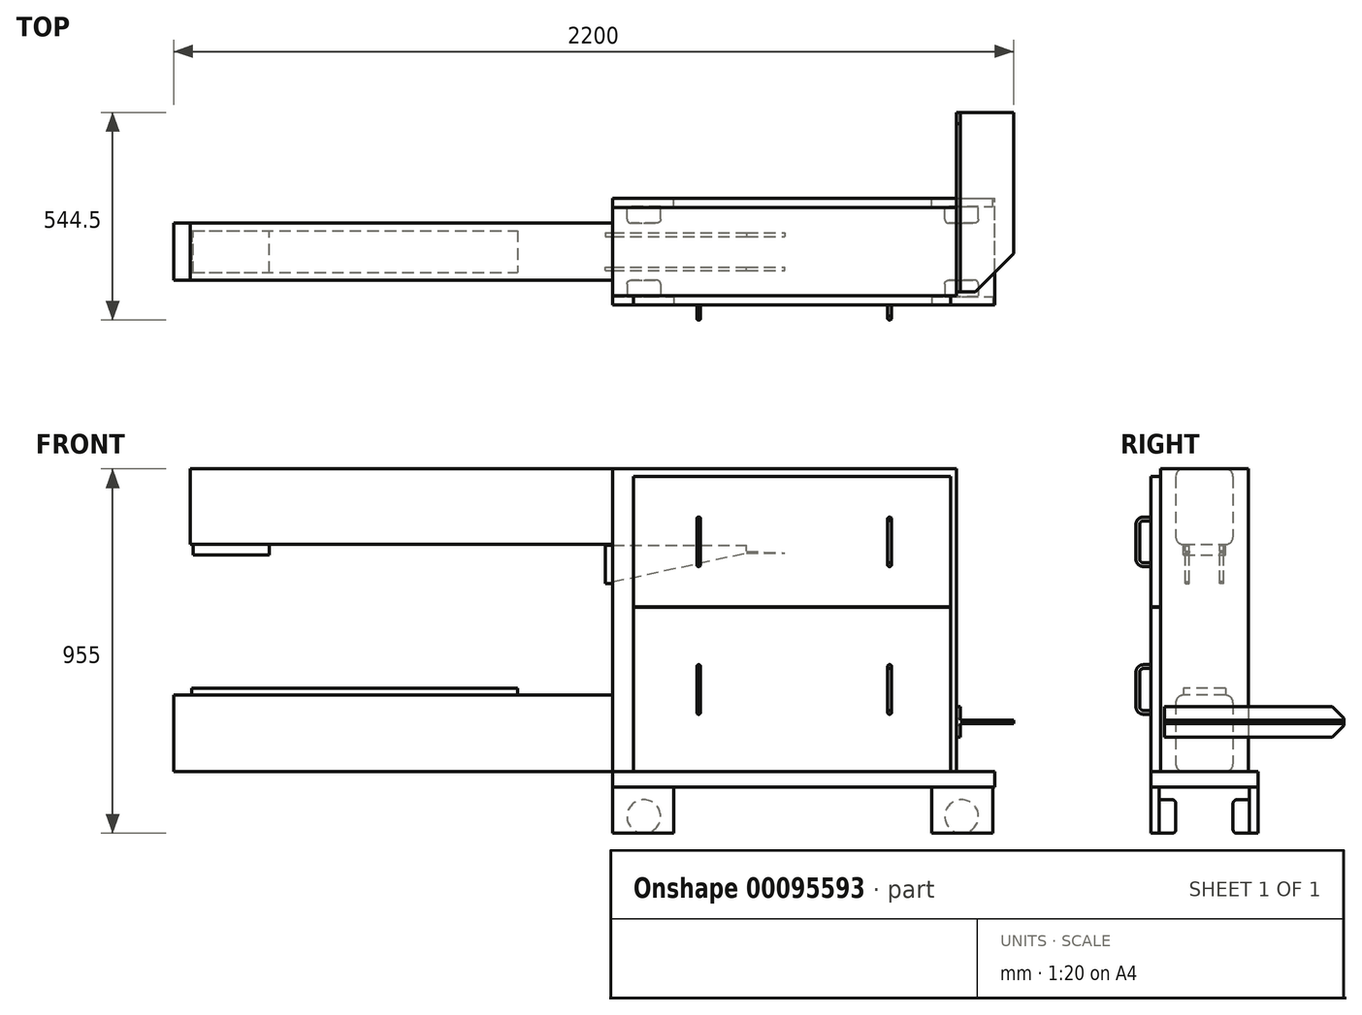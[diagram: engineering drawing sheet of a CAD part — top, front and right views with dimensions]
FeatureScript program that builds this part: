
annotation { "Feature Type Name" : "Feature", "Feature Type Description" : "" }
export const myFeature = defineFeature(function(context is Context, id is Id, definition is map)
    precondition{}
    {
        {
            var Q0;
            Q0=qCreatedBy(makeId("Front.planeOp"),FACE);
            var sketch = newSketch(context, id + "F0", { "sketchPlane" : qUnion([Q0])});
            skLineSegment(sketch, "E0.rect.bottom", {"start": v(-575, 100) * mm, "end": v(575, 100) * mm});
            skLineSegment(sketch, "E0.rect.top", {"start": v(-575, -100) * mm, "end": v(1475, -100) * mm});
            skLineSegment(sketch, "E0.rect.left", {"start": v(-575, 100) * mm, "end": v(-575, -100) * mm});
            skLineSegment(sketch, "E0.rect.right", {"start": v(575, 100) * mm, "end": v(575, -100) * mm});
            skPoint(sketch, "E0.rect.middle", {"position": v(0, 0) * mm});
            skLineSegment(sketch, "E1.0", {"start": v(-532, 495) * mm, "end": v(575, 495) * mm});
            skLineSegment(sketch, "E2.0", {"start": v(-532, 693) * mm, "end": v(1475, 693) * mm});
            skLineSegment(sketch, "E3.0", {"start": v(-532, 693) * mm, "end": v(-532, 495) * mm});
            skLineSegment(sketch, "E4", {"start": v(575, 693) * mm, "end": v(575, -100) * mm});
            skLineSegment(sketch, "E5.0", {"start": v(1475, 693) * mm, "end": v(1475, -100) * mm});
            skSolve(sketch);
        }
        {
            var Q0;
            {var subQ3=sQuery(id+"F0.wireOp",EDGE,"E1.0");Q0=makeQuery(id+"F0.imprint","IMPRINT",FACE,{"disambiguationData":[TD([[makeQuery(id+"F0.imprint","IMPRINT",EDGE,{"derivedFrom":subQ3}),1.0]])]});}
            var Q1;
            {var subQ3=sQuery(id+"F0.wireOp",EDGE,"E0.rect.bottom");Q1=makeQuery(id+"F0.imprint","IMPRINT",FACE,{"disambiguationData":[TD([[makeQuery(id+"F0.imprint","IMPRINT",EDGE,{"derivedFrom":subQ3}),-1.0]])]});}
            extrude(context, id + "F1", {"entities" : qUnion([Q0, Q1]), "endBound" : BoundingType.SYMMETRIC, "depth" : 150 * mm});
        }
        {
            var Q0;
            {var subQ0=sQuery(id+"F0.wireOp",EDGE,"E5.0");Q0=makeQuery(id+"F0.imprint","IMPRINT",FACE,{"disambiguationData":[TD([[makeQuery(id+"F0.imprint","IMPRINT",EDGE,{"derivedFrom":subQ0}),-1.0]])]});}
            extrude(context, id + "F2", {"entities" : qUnion([Q0]), "endBound" : BoundingType.SYMMETRIC, "depth" : 230 * mm});
        }
        {
            var Q0;
            Q0=makeQuery(id+"F1.opExtrude","CAP_EDGE",EDGE,{"disambiguationData":[OSD([sQuery(id+"F0.wireOp",EDGE,"E0.rect.bottom")])],"isStart":false});
            var Q1;
            Q1=makeQuery(id+"F1.opExtrude","CAP_EDGE",EDGE,{"disambiguationData":[OSD([sQuery(id+"F0.wireOp",EDGE,"E0.rect.top")])],"isStart":false});
            var Q2;
            Q2=makeQuery(id+"F1.opExtrude","CAP_EDGE",EDGE,{"disambiguationData":[OSD([sQuery(id+"F0.wireOp",EDGE,"E1.0")])],"isStart":false});
            var Q3;
            Q3=makeQuery(id+"F1.opExtrude","CAP_EDGE",EDGE,{"disambiguationData":[OSD([sQuery(id+"F0.wireOp",EDGE,"E2.0")])],"isStart":false});
            var Q4;
            Q4=makeQuery(id+"F1.opExtrude","CAP_EDGE",EDGE,{"disambiguationData":[OSD([sQuery(id+"F0.wireOp",EDGE,"E2.0")])],"isStart":true});
            var Q5;
            Q5=makeQuery(id+"F1.opExtrude","CAP_EDGE",EDGE,{"disambiguationData":[OSD([sQuery(id+"F0.wireOp",EDGE,"E1.0")])],"isStart":true});
            var Q6;
            Q6=makeQuery(id+"F1.opExtrude","CAP_EDGE",EDGE,{"disambiguationData":[OSD([sQuery(id+"F0.wireOp",EDGE,"E0.rect.bottom")])],"isStart":true});
            var Q7;
            Q7=makeQuery(id+"F1.opExtrude","CAP_EDGE",EDGE,{"disambiguationData":[OSD([sQuery(id+"F0.wireOp",EDGE,"E0.rect.top")])],"isStart":true});
            fillet(context, id + "F3", {"entities" : qUnion([Q0, Q1, Q2, Q3, Q4, Q5, Q6, Q7]), "radius" : 20 * mm, "tangentPropagation" : true, "allowEdgeOverflow" : false});
        }
        {
            var Q0;
            Q0=makeQuery(id+"F1.opExtrude","SWEPT_FACE",FACE,{"disambiguationData":[OSD([sQuery(id+"F0.wireOp",EDGE,"E0.rect.bottom")])]});
            var sketch = newSketch(context, id + "F4", { "sketchPlane" : qUnion([Q0])});
            skLineSegment(sketch, "E6.0", {"start": v(-528, -55) * mm, "end": v(-528, 55) * mm, "construction": true});
            skLineSegment(sketch, "E7.0", {"start": v(326, -55) * mm, "end": v(326, 55) * mm, "construction": true});
            skLineSegment(sketch, "E8.bottom", {"start": v(-528, 55) * mm, "end": v(326, 55) * mm});
            skLineSegment(sketch, "E8.top", {"start": v(-528, -55) * mm, "end": v(326, -55) * mm});
            skLineSegment(sketch, "E8.left", {"start": v(-528, 55) * mm, "end": v(-528, -55) * mm});
            skLineSegment(sketch, "E8.right", {"start": v(326, 55) * mm, "end": v(326, -55) * mm});
            skSolve(sketch);
        }
        {
            var Q0;
            Q0=qSketchRegion(id+"F4",true);
            extrude(context, id + "F5", {"entities" : qUnion([Q0]), "operationType" : NewBodyOperationType.ADD, "depth" : 18 * mm});
        }
        {
            var Q0;
            Q0=makeQuery(id+"F1.opExtrude","SWEPT_FACE",FACE,{"disambiguationData":[OSD([sQuery(id+"F0.wireOp",EDGE,"E1.0")])]});
            var sketch = newSketch(context, id + "F6", { "sketchPlane" : qUnion([Q0])});
            skLineSegment(sketch, "E9.0", {"start": v(-524, 55) * mm, "end": v(-524, -55) * mm, "construction": true});
            skLineSegment(sketch, "E10.0", {"start": v(-324, 55) * mm, "end": v(-324, -55) * mm, "construction": true});
            skLineSegment(sketch, "E11.bottom", {"start": v(-524, 55) * mm, "end": v(-324, 55) * mm});
            skLineSegment(sketch, "E11.top", {"start": v(-524, -55) * mm, "end": v(-324, -55) * mm});
            skLineSegment(sketch, "E11.left", {"start": v(-524, 55) * mm, "end": v(-524, -55) * mm});
            skLineSegment(sketch, "E11.right", {"start": v(-324, 55) * mm, "end": v(-324, -55) * mm});
            skSolve(sketch);
        }
        {
            var Q0;
            Q0=qSketchRegion(id+"F6",true);
            extrude(context, id + "F7", {"entities" : qUnion([Q0]), "operationType" : NewBodyOperationType.ADD, "depth" : 27 * mm});
        }
        {
            var Q0;
            Q0=qCreatedBy(makeId("Front.planeOp"),FACE);
            cPlane(context, id + "F8", {"entities" : qUnion([Q0]), "cplaneType" : CPlaneType.OFFSET, "offset" : 40 * mm, "width" : 150 * mm, "height" : 150 * mm});
        }
        {
            var Q0;
            Q0=qCreatedBy(id+"F8.planeOp",FACE);
            var sketch = newSketch(context, id + "F9", { "sketchPlane" : qUnion([Q0])});
            skLineSegment(sketch, "E12.0", {"start": v(-532, 495) * mm, "end": v(575, 495) * mm, "construction": true});
            skLineSegment(sketch, "E13.0", {"start": v(575, 693) * mm, "end": v(575, -100) * mm, "construction": true});
            skLineSegment(sketch, "E14.0", {"start": v(-575, 100) * mm, "end": v(575, 100) * mm, "construction": true});
            skLineSegment(sketch, "E15.0", {"start": v(475, 693) * mm, "end": v(475, -100) * mm, "construction": true});
            skLineSegment(sketch, "E16.0", {"start": v(-1025.5, 200) * mm, "end": v(1025.5, 200) * mm, "construction": true});
            skLineSegment(sketch, "E17", {"start": v(575, 296.5) * mm, "end": v(528.06, 296.5) * mm, "construction": true});
            skLineSegment(sketch, "E18.bottom", {"start": v(555, 200) * mm, "end": v(575, 200) * mm});
            skLineSegment(sketch, "E18.top", {"start": v(575, 100) * mm, "end": v(925.5, 100) * mm});
            skLineSegment(sketch, "E18.left", {"start": v(925.5, 120) * mm, "end": v(925.5, 100) * mm});
            skLineSegment(sketch, "E18.right", {"start": v(575, 200) * mm, "end": v(575, 100) * mm, "construction": true});
            skLineSegment(sketch, "E19.0", {"start": v(555, 200) * mm, "end": v(555, 100) * mm, "construction": true});
            skLineSegment(sketch, "E20.0", {"start": v(925.5, 120) * mm, "end": v(1025.5, 120) * mm, "construction": true});
            skLineSegment(sketch, "E21", {"start": v(555, 100) * mm, "end": v(1025.5, 120) * mm});
            skLineSegment(sketch, "E22", {"start": v(555, 200) * mm, "end": v(925.5, 120) * mm});
            skLineSegment(sketch, "E23", {"start": v(1025.5, 200) * mm, "end": v(1025.5, 120) * mm});
            skLineSegment(sketch, "E24.MirrorCS", {"start": v(555, 393) * mm, "end": v(575, 393) * mm});
            skLineSegment(sketch, "E25.MirrorCS", {"start": v(555, 493) * mm, "end": v(1025.5, 473) * mm});
            skLineSegment(sketch, "E26.MirrorCS", {"start": v(925.5, 473) * mm, "end": v(925.5, 493) * mm});
            skLineSegment(sketch, "E27.MirrorCS", {"start": v(575, 393) * mm, "end": v(575, 493) * mm});
            skLineSegment(sketch, "E28.MirrorCS", {"start": v(1025.5, 393) * mm, "end": v(1025.5, 473) * mm});
            skLineSegment(sketch, "E29.MirrorCS", {"start": v(555, 393) * mm, "end": v(925.5, 473) * mm});
            skLineSegment(sketch, "E30.MirrorCS", {"start": v(925.5, 473) * mm, "end": v(1025.5, 473) * mm});
            skLineSegment(sketch, "E31.MirrorCS", {"start": v(575, 493) * mm, "end": v(925.5, 493) * mm});
            skLineSegment(sketch, "E32.MirrorCS", {"start": v(555, 393) * mm, "end": v(555, 493) * mm});
            skSolve(sketch);
        }
        {
            var Q0;
            Q0=qSketchRegion(id+"F9",true);
            extrude(context, id + "F10", {"entities" : qUnion([Q0]), "depth" : 10 * mm});
        }
        {
            var Q0;
            Q0=makeQuery(id+"F10.opExtrude","SWEPT_BODY",BODY,{"disambiguationData":[OSD([sQuery(id+"F9.wireOp",EDGE,"E24.MirrorCS"),sQuery(id+"F9.wireOp",EDGE,"E26.MirrorCS"),sQuery(id+"F9.wireOp",EDGE,"E27.MirrorCS"),sQuery(id+"F9.wireOp",EDGE,"E28.MirrorCS"),sQuery(id+"F9.wireOp",EDGE,"E29.MirrorCS"),sQuery(id+"F9.wireOp",EDGE,"E31.MirrorCS")])]});
            var Q1;
            Q1=makeQuery(id+"F10.opExtrude","SWEPT_BODY",BODY,{"disambiguationData":[OSD([sQuery(id+"F9.wireOp",EDGE,"E18.bottom"),sQuery(id+"F9.wireOp",EDGE,"E18.top"),sQuery(id+"F9.wireOp",EDGE,"E18.left"),sQuery(id+"F9.wireOp",EDGE,"E21"),sQuery(id+"F9.wireOp",EDGE,"E22"),sQuery(id+"F9.wireOp",EDGE,"E23")])]});
            var Q2;
            Q2=qCreatedBy(makeId("Front.planeOp"),FACE);
            mirror(context, id + "F11", {"entities" : qUnion([Q0, Q1]), "mirrorPlane" : qUnion([Q2])});
        }
        {
            var Q0;
            Q0=makeQuery(id+"F2.opExtrude","CAP_FACE",FACE,{"disambiguationData":[OSD([sQuery(id+"F0.wireOp",EDGE,"E0.rect.top"),sQuery(id+"F0.wireOp",EDGE,"E2.0"),sQuery(id+"F0.wireOp",EDGE,"E4"),sQuery(id+"F0.wireOp",EDGE,"E5.0")])],"isStart":false});
            var sketch = newSketch(context, id + "F12", { "sketchPlane" : qUnion([Q0])});
            skLineSegment(sketch, "E33.0", {"start": v(-982.5, 673) * mm, "end": v(1925.5, 673) * mm});
            skLineSegment(sketch, "E34.0", {"start": v(-982.5, 331) * mm, "end": v(1925.5, 331) * mm});
            skLineSegment(sketch, "E35.0", {"start": v(-982.5, 330) * mm, "end": v(1925.5, 330) * mm});
            skLineSegment(sketch, "E36.0", {"start": v(570, 698) * mm, "end": v(570, -105) * mm});
            skLineSegment(sketch, "E36.1", {"start": v(1480, 698) * mm, "end": v(570, 698) * mm});
            skLineSegment(sketch, "E36.2", {"start": v(1480, -105) * mm, "end": v(1480, 698) * mm});
            skLineSegment(sketch, "E36.3", {"start": v(570, -105) * mm, "end": v(1480, -105) * mm});
            skLineSegment(sketch, "E37.0", {"start": v(-982.5, -108) * mm, "end": v(1925.5, -108) * mm});
            skLineSegment(sketch, "E38.0", {"start": v(629, 693) * mm, "end": v(629, -100) * mm});
            skLineSegment(sketch, "E39.0", {"start": v(1460, -105) * mm, "end": v(1460, 698) * mm});
            skSolve(sketch);
        }
        {
            var Q0;
            {var subQ3=sQuery(id+"F12.wireOp",EDGE,"E33.0");var subQ5=sQuery(id+"F12.wireOp",EDGE,"E38.0");var subQ7=makeQuery(id+"F12.imprint","INTERSECT",VERTEX,{"derivedFrom":[subQ3,subQ5]});Q0=makeQuery(id+"F12.imprint","IMPRINT",FACE,{"disambiguationData":[TD([[makeQuery(id+"F12.imprint","IMPRINT",EDGE,{"disambiguationData":[TD([[subQ7,-1.0]])],"derivedFrom":subQ3}),-1.0]])]});}
            var Q1;
            {var subQ3=sQuery(id+"F12.wireOp",EDGE,"E38.0");var subQ5=sQuery(id+"F12.wireOp",EDGE,"E35.0");var subQ7=makeQuery(id+"F12.imprint","INTERSECT",VERTEX,{"derivedFrom":[subQ5,subQ3]});Q1=makeQuery(id+"F12.imprint","IMPRINT",FACE,{"disambiguationData":[TD([[makeQuery(id+"F12.imprint","IMPRINT",EDGE,{"disambiguationData":[TD([[subQ7,-1.0]])],"derivedFrom":subQ5}),-1.0]])]});}
            extrude(context, id + "F13", {"entities" : qUnion([Q0, Q1]), "operationType" : NewBodyOperationType.ADD, "depth" : 25 * mm});
        }
        {
            var Q0;
            Q0=makeQuery(id+"F2.opExtrude","SWEPT_FACE",FACE,{"disambiguationData":[OSD([sQuery(id+"F0.wireOp",EDGE,"E5.0")])]});
            cPlane(context, id + "F14", {"entities" : qUnion([Q0]), "cplaneType" : CPlaneType.OFFSET, "offset" : 175 * mm, "oppositeDirection" : true, "width" : 150 * mm, "height" : 150 * mm});
        }
        {
            var Q0;
            Q0=qCreatedBy(id+"F14.planeOp",FACE);
            cPlane(context, id + "F15", {"entities" : qUnion([Q0]), "cplaneType" : CPlaneType.OFFSET, "offset" : 250 * mm, "oppositeDirection" : true, "width" : 150 * mm, "height" : 150 * mm});
        }
        {
            var Q0;
            Q0=qCreatedBy(id+"F14.planeOp",FACE);
            var sketch = newSketch(context, id + "F16", { "sketchPlane" : qUnion([Q0])});
            skLineSegment(sketch, "E40.0", {"start": v(-140, 331) * mm, "end": v(-140, 673) * mm, "construction": true});
            skLineSegment(sketch, "E41.0", {"start": v(-140, -100) * mm, "end": v(-140, 330) * mm, "construction": true});
            skLineSegment(sketch, "E42", {"start": v(-140, 502) * mm, "end": v(-356.24, 502) * mm, "construction": true});
            skLineSegment(sketch, "E43", {"start": v(-140, 115) * mm, "end": v(-344.44, 115) * mm, "construction": true});
            skLineSegment(sketch, "E44.0", {"start": v(-140, 562) * mm, "end": v(-159.5, 562) * mm});
            skLineSegment(sketch, "E45.0", {"start": v(-140, 175) * mm, "end": v(-344.44, 175) * mm, "construction": true});
            skLineSegment(sketch, "E46.0", {"start": v(-174.5, 502) * mm, "end": v(-174.5, 562) * mm, "construction": true});
            skLineSegment(sketch, "E47", {"start": v(-174.5, 160) * mm, "end": v(-174.5, 115) * mm});
            skLineSegment(sketch, "E48", {"start": v(-159.5, 175) * mm, "end": v(-140, 175) * mm});
            skLineSegment(sketch, "E49", {"start": v(-174.5, 502) * mm, "end": v(-174.5, 547) * mm});
            skPoint(sketch, "E50.visualSharp", {"position": v(-174.5, 175) * mm});
            skArc(sketch, "E50.filletArc", {"start": v(-159.5, 175) * mm, "mid": v(-170.1, 170.6) * mm, "end": v(-174.5, 160) * mm});
            skArc(sketch, "E51.filletArc", {"start": v(-159.5, 562) * mm, "mid": v(-170.1, 557.6) * mm, "end": v(-174.5, 547) * mm});
            skLineSegment(sketch, "E52.MirrorCS", {"start": v(-174.5, 502) * mm, "end": v(-174.5, 457) * mm});
            skLineSegment(sketch, "E53.MirrorCS", {"start": v(-140, 442) * mm, "end": v(-159.5, 442) * mm});
            skArc(sketch, "E54.MirrorCS", {"start": v(-159.5, 442) * mm, "mid": v(-170.1, 446.4) * mm, "end": v(-174.5, 457) * mm});
            skPoint(sketch, "E55.orphan", {"position": v(-174.5, 442) * mm});
            skArc(sketch, "E56.MirrorCS", {"start": v(-159.5, 55) * mm, "mid": v(-170.1, 59.4) * mm, "end": v(-174.5, 70) * mm});
            skPoint(sketch, "E57.MirrorP", {"position": v(-174.5, 55) * mm});
            skLineSegment(sketch, "E58.MirrorCS", {"start": v(-159.5, 55) * mm, "end": v(-140, 55) * mm});
            skLineSegment(sketch, "E59.MirrorCS", {"start": v(-174.5, 70) * mm, "end": v(-174.5, 115) * mm});
            skSolve(sketch);
        }
        {
            var Q0;
            Q0=makeQuery(id+"F13.opExtrude","CAP_FACE",FACE,{"disambiguationData":[OSD([sQuery(id+"F12.wireOp",EDGE,"E33.0"),sQuery(id+"F12.wireOp",EDGE,"E34.0"),sQuery(id+"F12.wireOp",EDGE,"E38.0"),sQuery(id+"F12.wireOp",EDGE,"E39.0")])],"isStart":false});
            var sketch = newSketch(context, id + "F17", { "sketchPlane" : qUnion([Q0])});
            skPoint(sketch, "E60.0", {"position": v(1300, 562) * mm});
            skPoint(sketch, "E61.0", {"position": v(1300, 175) * mm});
            skCircle(sketch, "E62", {"center": v(1300, 562) * mm, "radius": 5 * mm});
            skCircle(sketch, "E63", {"center": v(1300, 175) * mm, "radius": 5 * mm});
            skSolve(sketch);
        }
        {
            var Q0;
            Q0=makeQuery(id+"F17.imprint","IMPRINT",FACE,{"disambiguationData":[TD([[makeQuery(id+"F17.imprint","IMPRINT",EDGE,{"derivedFrom":sQuery(id+"F17.wireOp",EDGE,"E62")}),1.0]])]});
            var Q1;
            Q1=sQuery(id+"F16.wireOp",EDGE,"E44.0");
            var Q2;
            Q2=sQuery(id+"F16.wireOp",EDGE,"E51.filletArc");
            var Q3;
            Q3=sQuery(id+"F16.wireOp",EDGE,"E49");
            var Q4;
            Q4=sQuery(id+"F16.wireOp",EDGE,"E52.MirrorCS");
            var Q5;
            Q5=sQuery(id+"F16.wireOp",EDGE,"E54.MirrorCS");
            var Q6;
            Q6=sQuery(id+"F16.wireOp",EDGE,"E53.MirrorCS");
            sweep(context, id + "F18", {"profiles" : qUnion([Q0]), "path" : qUnion([Q1, Q2, Q3, Q4, Q5, Q6])});
        }
        {
            var Q0;
            Q0=makeQuery(id+"F17.imprint","IMPRINT",FACE,{"disambiguationData":[TD([[makeQuery(id+"F17.imprint","IMPRINT",EDGE,{"derivedFrom":sQuery(id+"F17.wireOp",EDGE,"E63")}),1.0]])]});
            var Q1;
            Q1=sQuery(id+"F16.wireOp",EDGE,"E48");
            var Q2;
            Q2=sQuery(id+"F16.wireOp",EDGE,"E50.filletArc");
            var Q3;
            Q3=sQuery(id+"F16.wireOp",EDGE,"E47");
            var Q4;
            Q4=sQuery(id+"F16.wireOp",EDGE,"E59.MirrorCS");
            var Q5;
            Q5=sQuery(id+"F16.wireOp",EDGE,"E56.MirrorCS");
            var Q6;
            Q6=sQuery(id+"F16.wireOp",EDGE,"E58.MirrorCS");
            sweep(context, id + "F19", {"profiles" : qUnion([Q0]), "path" : qUnion([Q1, Q2, Q3, Q4, Q5, Q6])});
        }
        {
            var Q0;
            Q0=makeQuery(id+"F19.opSweep","SWEPT_BODY",BODY,{"disambiguationData":[OSD([sQuery(id+"F16.wireOp",EDGE,"E58.MirrorCS"),sQuery(id+"F17.wireOp",EDGE,"E63")])]});
            var Q1;
            Q1=makeQuery(id+"F18.opSweep","SWEPT_BODY",BODY,{"disambiguationData":[OSD([sQuery(id+"F16.wireOp",EDGE,"E53.MirrorCS"),sQuery(id+"F17.wireOp",EDGE,"E62")])]});
            var Q2;
            Q2=qCreatedBy(id+"F15.planeOp",FACE);
            mirror(context, id + "F20", {"operationType" : NewBodyOperationType.ADD, "entities" : qUnion([Q0, Q1]), "mirrorPlane" : qUnion([Q2])});
        }
        {
            var Q0;
            Q0=makeQuery(id+"F2.opExtrude","SWEPT_FACE",FACE,{"disambiguationData":[OSD([sQuery(id+"F0.wireOp",EDGE,"E5.0")])]});
            cPlane(context, id + "F21", {"entities" : qUnion([Q0]), "cplaneType" : CPlaneType.OFFSET, "offset" : 100 * mm, "width" : 150 * mm, "height" : 150 * mm});
        }
        {
            var Q0;
            Q0=qCreatedBy(id+"F21.planeOp",FACE);
            var sketch = newSketch(context, id + "F22", { "sketchPlane" : qUnion([Q0])});
            skLineSegment(sketch, "E64", {"start": v(0, 0) * mm, "end": v(0, -281) * mm, "construction": true});
            skLineSegment(sketch, "E65.0", {"start": v(-140, 0) * mm, "end": v(-140, -277.75) * mm, "construction": true});
            skLineSegment(sketch, "E66.0.0", {"start": v(115, -100) * mm, "end": v(115, 693) * mm, "construction": true});
            skLineSegment(sketch, "E66.0.1", {"start": v(115, 693) * mm, "end": v(-115, 693) * mm, "construction": true});
            skLineSegment(sketch, "E66.0.2", {"start": v(-115, 693) * mm, "end": v(-115, -100) * mm, "construction": true});
            skLineSegment(sketch, "E66.0.3", {"start": v(-115, -100) * mm, "end": v(115, -100) * mm, "construction": true});
            skPoint(sketch, "E67.oppositeSnap0", {"position": v(0, -140.5) * mm});
            skLineSegment(sketch, "E67.bottom", {"start": v(-140, -100) * mm, "end": v(140, -100) * mm});
            skLineSegment(sketch, "E67.top", {"start": v(-140, -140.5) * mm, "end": v(140, -140.5) * mm});
            skLineSegment(sketch, "E67.left", {"start": v(-140, -100) * mm, "end": v(-140, -140.5) * mm});
            skLineSegment(sketch, "E67.right", {"start": v(140, -100) * mm, "end": v(140, -140.5) * mm});
            skSolve(sketch);
        }
        {
            var Q0;
            Q0=qSketchRegion(id+"F22",true);
            extrude(context, id + "F23", {"entities" : qUnion([Q0]), "oppositeDirection" : true, "depth" : 1000 * mm});
        }
        {
            var Q0;
            Q0=makeQuery(id+"F23.opExtrude","SWEPT_FACE",FACE,{"disambiguationData":[OSD([sQuery(id+"F22.wireOp",EDGE,"E67.left")])]});
            var sketch = newSketch(context, id + "F24", { "sketchPlane" : qUnion([Q0])});
            skLineSegment(sketch, "E68.bottom", {"start": v(1570, -140.5) * mm, "end": v(1410, -140.5) * mm});
            skLineSegment(sketch, "E68.top", {"start": v(1570, -262) * mm, "end": v(1410, -262) * mm});
            skLineSegment(sketch, "E68.left", {"start": v(1570, -140.5) * mm, "end": v(1570, -262) * mm});
            skLineSegment(sketch, "E68.right", {"start": v(1410, -140.5) * mm, "end": v(1410, -262) * mm});
            skLineSegment(sketch, "E69.0.0", {"start": v(1575, -140.5) * mm, "end": v(1575, -100) * mm, "construction": true});
            skLineSegment(sketch, "E69.0.1", {"start": v(1575, -100) * mm, "end": v(575, -100) * mm, "construction": true});
            skLineSegment(sketch, "E69.0.2", {"start": v(575, -100) * mm, "end": v(575, -140.5) * mm, "construction": true});
            skLineSegment(sketch, "E69.0.3", {"start": v(575, -140.5) * mm, "end": v(1575, -140.5) * mm, "construction": true});
            skLineSegment(sketch, "E70.bottom", {"start": v(575, -140.5) * mm, "end": v(735, -140.5) * mm});
            skLineSegment(sketch, "E70.top", {"start": v(575, -262) * mm, "end": v(735, -262) * mm});
            skLineSegment(sketch, "E70.left", {"start": v(575, -140.5) * mm, "end": v(575, -262) * mm});
            skLineSegment(sketch, "E70.right", {"start": v(735, -140.5) * mm, "end": v(735, -262) * mm});
            skSolve(sketch);
        }
        {
            var Q0;
            Q0=qSketchRegion(id+"F24",true);
            extrude(context, id + "F25", {"entities" : qUnion([Q0]), "oppositeDirection" : true, "depth" : 22 * mm});
        }
        {
            var Q0;
            Q0=makeQuery(id+"F25.opExtrude","CAP_FACE",FACE,{"disambiguationData":[OSD([sQuery(id+"F24.wireOp",EDGE,"E70.bottom"),sQuery(id+"F24.wireOp",EDGE,"E70.top"),sQuery(id+"F24.wireOp",EDGE,"E70.left"),sQuery(id+"F24.wireOp",EDGE,"E70.right")])],"isStart":false});
            var sketch = newSketch(context, id + "F26", { "sketchPlane" : qUnion([Q0])});
            skLineSegment(sketch, "E71.0.0", {"start": v(-575, -262) * mm, "end": v(-575, -140.5) * mm, "construction": true});
            skLineSegment(sketch, "E71.0.1", {"start": v(-575, -140.5) * mm, "end": v(-735, -140.5) * mm, "construction": true});
            skLineSegment(sketch, "E71.0.2", {"start": v(-735, -140.5) * mm, "end": v(-735, -262) * mm, "construction": true});
            skLineSegment(sketch, "E71.0.3", {"start": v(-735, -262) * mm, "end": v(-575, -262) * mm, "construction": true});
            skLineSegment(sketch, "E72.0", {"start": v(-1185.5, -218) * mm, "end": v(-1791.8, -218) * mm, "construction": true});
            skCircle(sketch, "E73", {"center": v(-1488.65, -218) * mm, "radius": 44 * mm});
            skLineSegment(sketch, "E74.1.0", {"start": v(-1570, -262) * mm, "end": v(-1410, -262) * mm, "construction": true});
            skLineSegment(sketch, "E74.1.1", {"start": v(-1410, -262) * mm, "end": v(-1410, -140.5) * mm, "construction": true});
            skLineSegment(sketch, "E74.1.2", {"start": v(-1410, -140.5) * mm, "end": v(-1570, -140.5) * mm, "construction": true});
            skLineSegment(sketch, "E74.1.3", {"start": v(-1570, -140.5) * mm, "end": v(-1570, -262) * mm, "construction": true});
            skLineSegment(sketch, "E75", {"start": v(-1410, -201.25) * mm, "end": v(-735, -201.25) * mm, "construction": true});
            skLineSegment(sketch, "E76", {"start": v(-1072.5, -201.25) * mm, "end": v(-1072.5, -366.76) * mm, "construction": true});
            skCircle(sketch, "E77.MirrorC", {"center": v(-656.35, -218) * mm, "radius": 44 * mm});
            skSolve(sketch);
        }
        {
            var Q0;
            Q0=qSketchRegion(id+"F26",true);
            extrude(context, id + "F27", {"entities" : qUnion([Q0]), "depth" : 43 * mm});
        }
        {
            var Q0;
            Q0=makeQuery(id+"F27.opExtrude","CAP_FACE",FACE,{"disambiguationData":[OSD([sQuery(id+"F26.wireOp",EDGE,"E73")])],"isStart":false});
            var Q1;
            Q1=makeQuery(id+"F27.opExtrude","CAP_FACE",FACE,{"disambiguationData":[OSD([sQuery(id+"F26.wireOp",EDGE,"E77.MirrorC")])],"isStart":false});
            fillet(context, id + "F28", {"entities" : qUnion([Q0, Q1]), "radius" : 10 * mm, "tangentPropagation" : true, "allowEdgeOverflow" : false});
        }
        {
            var Q0;
            Q0=makeQuery(id+"F25.opExtrude","SWEPT_BODY",BODY,{"disambiguationData":[OSD([sQuery(id+"F24.wireOp",EDGE,"E68.bottom"),sQuery(id+"F24.wireOp",EDGE,"E68.top"),sQuery(id+"F24.wireOp",EDGE,"E68.left"),sQuery(id+"F24.wireOp",EDGE,"E68.right")])]});
            var Q1;
            Q1=makeQuery(id+"F25.opExtrude","SWEPT_BODY",BODY,{"disambiguationData":[OSD([sQuery(id+"F24.wireOp",EDGE,"E70.bottom"),sQuery(id+"F24.wireOp",EDGE,"E70.top"),sQuery(id+"F24.wireOp",EDGE,"E70.left"),sQuery(id+"F24.wireOp",EDGE,"E70.right")])]});
            var Q2;
            Q2=makeQuery(id+"F27.opExtrude","SWEPT_BODY",BODY,{"disambiguationData":[OSD([sQuery(id+"F26.wireOp",EDGE,"E77.MirrorC")])]});
            var Q3;
            Q3=makeQuery(id+"F27.opExtrude","SWEPT_BODY",BODY,{"disambiguationData":[OSD([sQuery(id+"F26.wireOp",EDGE,"E73")])]});
            var Q4;
            Q4=qCreatedBy(makeId("Front.planeOp"),FACE);
            mirror(context, id + "F29", {"entities" : qUnion([Q0, Q1, Q2, Q3]), "mirrorPlane" : qUnion([Q4])});
        }
        {
            var Q0;
            Q0=makeQuery(id+"F2.opExtrude","SWEPT_FACE",FACE,{"disambiguationData":[OSD([sQuery(id+"F0.wireOp",EDGE,"E5.0")])]});
            var sketch = newSketch(context, id + "F30", { "sketchPlane" : qUnion([Q0])});
            skLineSegment(sketch, "E78.0", {"start": v(-140, -100) * mm, "end": v(140, -100) * mm, "construction": true});
            skLineSegment(sketch, "E79.0", {"start": v(-105, -10) * mm, "end": v(365, -10) * mm});
            skLineSegment(sketch, "E80.0", {"start": v(-105, 70) * mm, "end": v(365, 70) * mm});
            skLineSegment(sketch, "E81.0", {"start": v(365, 70) * mm, "end": v(365, -10) * mm});
            skLineSegment(sketch, "E82.0", {"start": v(-105, 70) * mm, "end": v(-105, -10) * mm});
            skSolve(sketch);
        }
        {
            var Q0;
            Q0=qSketchRegion(id+"F30",true);
            extrude(context, id + "F31", {"entities" : qUnion([Q0]), "operationType" : NewBodyOperationType.ADD, "depth" : 10 * mm});
        }
        {
            var Q0;
            Q0=makeQuery(id+"F31.opExtrude","SWEPT_EDGE",EDGE,{"disambiguationData":[OSD([sQuery(id+"F30.wireOp",EDGE,"E80.0"),sQuery(id+"F30.wireOp",EDGE,"E81.0")])]});
            var Q1;
            Q1=makeQuery(id+"F31.opExtrude","SWEPT_EDGE",EDGE,{"disambiguationData":[OSD([sQuery(id+"F30.wireOp",EDGE,"E79.0"),sQuery(id+"F30.wireOp",EDGE,"E81.0")])]});
            chamfer(context, id + "F32", {"entities" : qUnion([Q0, Q1]), "width" : 30 * mm, "tangentPropagation" : true});
        }
        {
            var Q0;
            Q0=makeQuery(id+"F31.opExtrude","CAP_FACE",FACE,{"disambiguationData":[OSD([sQuery(id+"F30.wireOp",EDGE,"E79.0"),sQuery(id+"F30.wireOp",EDGE,"E80.0"),sQuery(id+"F30.wireOp",EDGE,"E81.0"),sQuery(id+"F30.wireOp",EDGE,"E82.0")])],"isStart":false});
            var sketch = newSketch(context, id + "F33", { "sketchPlane" : qUnion([Q0])});
            skLineSegment(sketch, "E83", {"start": v(365, 30) * mm, "end": v(-105, 30) * mm, "construction": true});
            skLineSegment(sketch, "E84.0", {"start": v(365, 35) * mm, "end": v(-105, 35) * mm});
            skLineSegment(sketch, "E85.0", {"start": v(365, 25) * mm, "end": v(-105, 25) * mm});
            skLineSegment(sketch, "E86", {"start": v(-105, 35) * mm, "end": v(-105, 25) * mm});
            skLineSegment(sketch, "E87", {"start": v(365, 35) * mm, "end": v(365, 25) * mm});
            skSolve(sketch);
        }
        {
            var Q0;
            Q0=qSketchRegion(id+"F33",true);
            extrude(context, id + "F34", {"entities" : qUnion([Q0]), "operationType" : NewBodyOperationType.ADD, "depth" : 140 * mm});
        }
        {
            var Q0;
            Q0=makeQuery(id+"F34.opExtrude","CAP_EDGE",EDGE,{"disambiguationData":[OSD([sQuery(id+"F33.wireOp",EDGE,"E86")])],"isStart":false});
            chamfer(context, id + "F35", {"entities" : qUnion([Q0]), "width" : 100 * mm, "tangentPropagation" : true});
        }
    });
